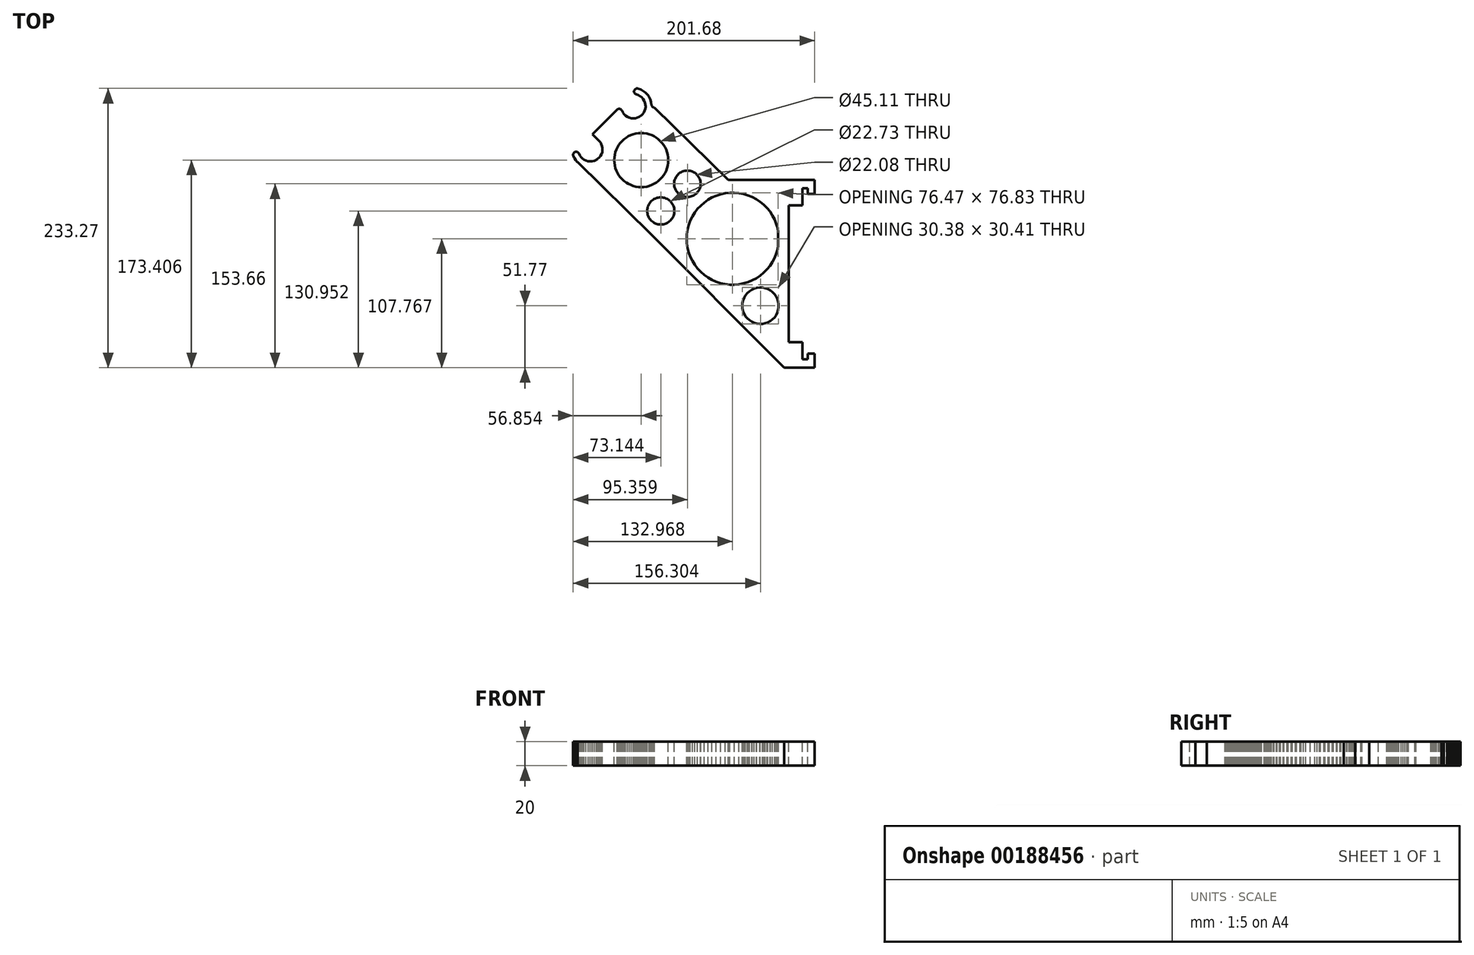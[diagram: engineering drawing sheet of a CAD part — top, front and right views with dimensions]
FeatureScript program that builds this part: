
annotation { "Feature Type Name" : "Feature", "Feature Type Description" : "" }
export const myFeature = defineFeature(function(context is Context, id is Id, definition is map)
    precondition{}
    {
        {
            var Q0;
            Q0=qCreatedBy(makeId("Top.planeOp"),FACE);
            var sketch = newSketch(context, id + "F0", { "sketchPlane" : qUnion([Q0])});
            skLineSegment(sketch, "E0", {"start": v(39.12, 12.68) * mm, "end": v(39.7, 15.67) * mm});
            skLineSegment(sketch, "E1", {"start": v(39.7, 15.67) * mm, "end": v(39.7, 16.24) * mm});
            skLineSegment(sketch, "E2", {"start": v(39.7, 16.24) * mm, "end": v(39.7, 16.28) * mm});
            skLineSegment(sketch, "E3", {"start": v(39.7, 16.28) * mm, "end": v(39.7, 16.48) * mm});
            skLineSegment(sketch, "E4", {"start": v(39.7, 16.48) * mm, "end": v(39.7, 16.55) * mm});
            skLineSegment(sketch, "E5", {"start": v(39.7, 16.55) * mm, "end": v(39.7, 16.6) * mm});
            skLineSegment(sketch, "E6", {"start": v(39.7, 16.6) * mm, "end": v(39.7, 16.7) * mm});
            skLineSegment(sketch, "E7", {"start": v(39.7, 16.7) * mm, "end": v(39.7, 16.8) * mm});
            skLineSegment(sketch, "E8", {"start": v(39.7, 16.8) * mm, "end": v(39.7, 16.95) * mm});
            skLineSegment(sketch, "E9", {"start": v(39.7, 16.95) * mm, "end": v(39.7, 17.21) * mm});
            skLineSegment(sketch, "E10", {"start": v(39.7, 17.21) * mm, "end": v(39.7, 17.9) * mm});
            skLineSegment(sketch, "E11", {"start": v(39.7, 17.9) * mm, "end": v(39.7, 18.04) * mm});
            skLineSegment(sketch, "E12", {"start": v(39.7, 18.04) * mm, "end": v(39.7, 18.74) * mm});
            skLineSegment(sketch, "E13", {"start": v(39.7, 18.74) * mm, "end": v(39.7, 21.09) * mm});
            skLineSegment(sketch, "E14", {"start": v(39.7, 21.09) * mm, "end": v(39.7, 21.12) * mm});
            skLineSegment(sketch, "E15", {"start": v(39.7, 21.12) * mm, "end": v(39.7, 21.25) * mm});
            skLineSegment(sketch, "E16", {"start": v(39.7, 21.25) * mm, "end": v(39.7, 21.3) * mm});
            skLineSegment(sketch, "E17", {"start": v(39.7, 21.3) * mm, "end": v(39.7, 23.38) * mm});
            skLineSegment(sketch, "E18", {"start": v(39.7, 23.38) * mm, "end": v(39.7, 23.5) * mm});
            skLineSegment(sketch, "E19", {"start": v(39.7, 23.5) * mm, "end": v(39.7, 26.9) * mm});
            skLineSegment(sketch, "E20", {"start": v(39.7, 26.9) * mm, "end": v(39.7, 26.97) * mm});
            skLineSegment(sketch, "E21", {"start": v(39.7, 26.97) * mm, "end": v(39.12, 29.96) * mm});
            skLineSegment(sketch, "E22", {"start": v(39.12, 29.96) * mm, "end": v(38.07, 33.67) * mm});
            skLineSegment(sketch, "E23", {"start": v(38.07, 33.67) * mm, "end": v(36.64, 37.26) * mm});
            skLineSegment(sketch, "E24", {"start": v(36.64, 37.26) * mm, "end": v(34.87, 40.7) * mm});
            skLineSegment(sketch, "E25", {"start": v(34.87, 40.7) * mm, "end": v(32.75, 43.93) * mm});
            skLineSegment(sketch, "E26", {"start": v(32.75, 43.93) * mm, "end": v(30.33, 46.93) * mm});
            skLineSegment(sketch, "E27", {"start": v(30.33, 46.93) * mm, "end": v(27.61, 49.68) * mm});
            skLineSegment(sketch, "E28", {"start": v(27.61, 49.68) * mm, "end": v(24.64, 52.14) * mm});
            skLineSegment(sketch, "E29", {"start": v(24.64, 52.14) * mm, "end": v(21.43, 54.29) * mm});
            skLineSegment(sketch, "E30", {"start": v(21.43, 54.29) * mm, "end": v(18.02, 56.1) * mm});
            skLineSegment(sketch, "E31", {"start": v(18.02, 56.1) * mm, "end": v(14.45, 57.57) * mm});
            skLineSegment(sketch, "E32", {"start": v(14.45, 57.57) * mm, "end": v(10.74, 58.67) * mm});
            skLineSegment(sketch, "E33", {"start": v(10.74, 58.67) * mm, "end": v(6.95, 59.4) * mm});
            skLineSegment(sketch, "E34", {"start": v(6.95, 59.4) * mm, "end": v(3.1, 59.73) * mm});
            skLineSegment(sketch, "E35", {"start": v(3.1, 59.73) * mm, "end": v(-0.76, 59.68) * mm});
            skLineSegment(sketch, "E36", {"start": v(-0.76, 59.68) * mm, "end": v(-4.6, 59.24) * mm});
            skLineSegment(sketch, "E37", {"start": v(-4.6, 59.24) * mm, "end": v(-8.37, 58.42) * mm});
            skLineSegment(sketch, "E38", {"start": v(-8.37, 58.42) * mm, "end": v(-12.04, 57.23) * mm});
            skLineSegment(sketch, "E39", {"start": v(-12.04, 57.23) * mm, "end": v(-15.58, 55.67) * mm});
            skLineSegment(sketch, "E40", {"start": v(-15.58, 55.67) * mm, "end": v(-18.94, 53.77) * mm});
            skLineSegment(sketch, "E41", {"start": v(-18.94, 53.77) * mm, "end": v(-22.1, 51.54) * mm});
            skLineSegment(sketch, "E42", {"start": v(-22.1, 51.54) * mm, "end": v(-25, 49) * mm});
            skLineSegment(sketch, "E43", {"start": v(-25, 49) * mm, "end": v(-27.65, 46.19) * mm});
            skLineSegment(sketch, "E44", {"start": v(-27.65, 46.19) * mm, "end": v(-30, 43.12) * mm});
            skLineSegment(sketch, "E45", {"start": v(-30, 43.12) * mm, "end": v(-32.02, 39.83) * mm});
            skLineSegment(sketch, "E46", {"start": v(-32.02, 39.83) * mm, "end": v(-33.7, 36.36) * mm});
            skLineSegment(sketch, "E47", {"start": v(-33.7, 36.36) * mm, "end": v(-35.04, 32.73) * mm});
            skLineSegment(sketch, "E48", {"start": v(-35.04, 32.73) * mm, "end": v(-36, 29) * mm});
            skLineSegment(sketch, "E49", {"start": v(-36, 29) * mm, "end": v(-36.58, 25.17) * mm});
            skLineSegment(sketch, "E50", {"start": v(-36.58, 25.17) * mm, "end": v(-36.78, 21.32) * mm});
            skLineSegment(sketch, "E51", {"start": v(-36.78, 21.32) * mm, "end": v(-36.58, 17.46) * mm});
            skLineSegment(sketch, "E52", {"start": v(-36.58, 17.46) * mm, "end": v(-36, 13.64) * mm});
            skLineSegment(sketch, "E53", {"start": v(-36, 13.64) * mm, "end": v(-35.04, 9.9) * mm});
            skLineSegment(sketch, "E54", {"start": v(-35.04, 9.9) * mm, "end": v(-33.7, 6.27) * mm});
            skLineSegment(sketch, "E55", {"start": v(-33.7, 6.27) * mm, "end": v(-32.02, 2.8) * mm});
            skLineSegment(sketch, "E56", {"start": v(-32.02, 2.8) * mm, "end": v(-30, -0.49) * mm});
            skLineSegment(sketch, "E57", {"start": v(-30, -0.49) * mm, "end": v(-27.65, -3.55) * mm});
            skLineSegment(sketch, "E58", {"start": v(-27.65, -3.55) * mm, "end": v(-25, -6.37) * mm});
            skLineSegment(sketch, "E59", {"start": v(-25, -6.37) * mm, "end": v(-22.1, -8.9) * mm});
            skLineSegment(sketch, "E60", {"start": v(-22.1, -8.9) * mm, "end": v(-18.94, -11.14) * mm});
            skLineSegment(sketch, "E61", {"start": v(-18.94, -11.14) * mm, "end": v(-15.58, -13.04) * mm});
            skLineSegment(sketch, "E62", {"start": v(-15.58, -13.04) * mm, "end": v(-12.04, -14.6) * mm});
            skLineSegment(sketch, "E63", {"start": v(-12.04, -14.6) * mm, "end": v(-8.37, -15.8) * mm});
            skLineSegment(sketch, "E64", {"start": v(-8.37, -15.8) * mm, "end": v(-4.6, -16.61) * mm});
            skLineSegment(sketch, "E65", {"start": v(-4.6, -16.61) * mm, "end": v(-0.76, -17.05) * mm});
            skLineSegment(sketch, "E66", {"start": v(-0.76, -17.05) * mm, "end": v(3.1, -17.1) * mm});
            skLineSegment(sketch, "E67", {"start": v(3.1, -17.1) * mm, "end": v(6.95, -16.76) * mm});
            skLineSegment(sketch, "E68", {"start": v(6.95, -16.76) * mm, "end": v(10.74, -16.04) * mm});
            skLineSegment(sketch, "E69", {"start": v(10.74, -16.04) * mm, "end": v(14.45, -14.94) * mm});
            skLineSegment(sketch, "E70", {"start": v(14.45, -14.94) * mm, "end": v(18.02, -13.47) * mm});
            skLineSegment(sketch, "E71", {"start": v(18.02, -13.47) * mm, "end": v(21.43, -11.65) * mm});
            skLineSegment(sketch, "E72", {"start": v(21.43, -11.65) * mm, "end": v(24.64, -9.5) * mm});
            skLineSegment(sketch, "E73", {"start": v(24.64, -9.5) * mm, "end": v(27.61, -7.04) * mm});
            skLineSegment(sketch, "E74", {"start": v(27.61, -7.04) * mm, "end": v(30.33, -4.3) * mm});
            skLineSegment(sketch, "E75", {"start": v(30.33, -4.3) * mm, "end": v(32.75, -1.3) * mm});
            skLineSegment(sketch, "E76", {"start": v(32.75, -1.3) * mm, "end": v(34.87, 1.94) * mm});
            skLineSegment(sketch, "E77", {"start": v(34.87, 1.94) * mm, "end": v(36.64, 5.37) * mm});
            skLineSegment(sketch, "E78", {"start": v(36.64, 5.37) * mm, "end": v(38.07, 8.96) * mm});
            skLineSegment(sketch, "E79", {"start": v(38.07, 8.96) * mm, "end": v(39.12, 12.68) * mm});
            skLineSegment(sketch, "E80", {"start": v(-110.95, 88) * mm, "end": v(-110.88, 88.06) * mm});
            skLineSegment(sketch, "E81", {"start": v(-110.88, 88.06) * mm, "end": v(-109.69, 89.17) * mm});
            skLineSegment(sketch, "E82", {"start": v(-109.69, 89.17) * mm, "end": v(-109.62, 89.23) * mm});
            skLineSegment(sketch, "E83", {"start": v(-109.62, 89.23) * mm, "end": v(-108.63, 90.52) * mm});
            skLineSegment(sketch, "E84", {"start": v(-108.63, 90.52) * mm, "end": v(-108.58, 90.59) * mm});
            skLineSegment(sketch, "E85", {"start": v(-108.58, 90.59) * mm, "end": v(-107.82, 92.03) * mm});
            skLineSegment(sketch, "E86", {"start": v(-107.82, 92.03) * mm, "end": v(-107.78, 92.1) * mm});
            skLineSegment(sketch, "E87", {"start": v(-107.78, 92.1) * mm, "end": v(-107.28, 93.66) * mm});
            skLineSegment(sketch, "E88", {"start": v(-107.28, 93.66) * mm, "end": v(-107.25, 93.74) * mm});
            skLineSegment(sketch, "E89", {"start": v(-107.25, 93.74) * mm, "end": v(-107.01, 95.36) * mm});
            skLineSegment(sketch, "E90", {"start": v(-107.01, 95.36) * mm, "end": v(-107, 95.44) * mm});
            skLineSegment(sketch, "E91", {"start": v(-107, 95.44) * mm, "end": v(-107.04, 97.07) * mm});
            skLineSegment(sketch, "E92", {"start": v(-107.04, 97.07) * mm, "end": v(-107.04, 97.16) * mm});
            skLineSegment(sketch, "E93", {"start": v(-107.04, 97.16) * mm, "end": v(-107.36, 98.76) * mm});
            skLineSegment(sketch, "E94", {"start": v(-107.36, 98.76) * mm, "end": v(-107.37, 98.84) * mm});
            skLineSegment(sketch, "E95", {"start": v(-107.37, 98.84) * mm, "end": v(-107.95, 100.37) * mm});
            skLineSegment(sketch, "E96", {"start": v(-107.95, 100.37) * mm, "end": v(-107.98, 100.45) * mm});
            skLineSegment(sketch, "E97", {"start": v(-107.98, 100.45) * mm, "end": v(-108.8, 101.85) * mm});
            skLineSegment(sketch, "E98", {"start": v(-108.8, 101.85) * mm, "end": v(-108.85, 101.93) * mm});
            skLineSegment(sketch, "E99", {"start": v(-108.85, 101.93) * mm, "end": v(-109.9, 103.17) * mm});
            skLineSegment(sketch, "E100", {"start": v(-109.9, 103.17) * mm, "end": v(-109.96, 103.24) * mm});
            skLineSegment(sketch, "E101", {"start": v(-109.96, 103.24) * mm, "end": v(-110.23, 103.5) * mm});
            skLineSegment(sketch, "E102", {"start": v(-110.23, 103.5) * mm, "end": v(-115.35, 108.63) * mm});
            skLineSegment(sketch, "E103", {"start": v(-115.35, 108.63) * mm, "end": v(-114.32, 109.65) * mm});
            skLineSegment(sketch, "E104", {"start": v(-114.32, 109.65) * mm, "end": v(-94.84, 129.13) * mm});
            skLineSegment(sketch, "E105", {"start": v(-94.84, 129.13) * mm, "end": v(-94.52, 129.4) * mm});
            skLineSegment(sketch, "E106", {"start": v(-94.52, 129.4) * mm, "end": v(-94.16, 129.62) * mm});
            skLineSegment(sketch, "E107", {"start": v(-94.16, 129.62) * mm, "end": v(-93.77, 129.77) * mm});
            skLineSegment(sketch, "E108", {"start": v(-93.77, 129.77) * mm, "end": v(-93.36, 129.86) * mm});
            skLineSegment(sketch, "E109", {"start": v(-93.36, 129.86) * mm, "end": v(-92.94, 129.88) * mm});
            skLineSegment(sketch, "E110", {"start": v(-92.94, 129.88) * mm, "end": v(-92.53, 129.83) * mm});
            skLineSegment(sketch, "E111", {"start": v(-92.53, 129.83) * mm, "end": v(-92.12, 129.7) * mm});
            skLineSegment(sketch, "E112", {"start": v(-92.12, 129.7) * mm, "end": v(-91.75, 129.52) * mm});
            skLineSegment(sketch, "E113", {"start": v(-91.75, 129.52) * mm, "end": v(-91.4, 129.28) * mm});
            skLineSegment(sketch, "E114", {"start": v(-91.4, 129.28) * mm, "end": v(-91.1, 128.98) * mm});
            skLineSegment(sketch, "E115", {"start": v(-91.1, 128.98) * mm, "end": v(-90.87, 128.64) * mm});
            skLineSegment(sketch, "E116", {"start": v(-90.87, 128.64) * mm, "end": v(-90.68, 128.27) * mm});
            skLineSegment(sketch, "E117", {"start": v(-90.68, 128.27) * mm, "end": v(-89.95, 126.8) * mm});
            skLineSegment(sketch, "E118", {"start": v(-89.95, 126.8) * mm, "end": v(-89.91, 126.72) * mm});
            skLineSegment(sketch, "E119", {"start": v(-89.91, 126.72) * mm, "end": v(-88.95, 125.39) * mm});
            skLineSegment(sketch, "E120", {"start": v(-88.95, 125.39) * mm, "end": v(-88.9, 125.32) * mm});
            skLineSegment(sketch, "E121", {"start": v(-88.9, 125.32) * mm, "end": v(-87.72, 124.17) * mm});
            skLineSegment(sketch, "E122", {"start": v(-87.72, 124.17) * mm, "end": v(-87.66, 124.11) * mm});
            skLineSegment(sketch, "E123", {"start": v(-87.66, 124.11) * mm, "end": v(-86.3, 123.19) * mm});
            skLineSegment(sketch, "E124", {"start": v(-86.3, 123.19) * mm, "end": v(-86.23, 123.14) * mm});
            skLineSegment(sketch, "E125", {"start": v(-86.23, 123.14) * mm, "end": v(-84.74, 122.45) * mm});
            skLineSegment(sketch, "E126", {"start": v(-84.74, 122.45) * mm, "end": v(-84.66, 122.42) * mm});
            skLineSegment(sketch, "E127", {"start": v(-84.66, 122.42) * mm, "end": v(-83.07, 122) * mm});
            skLineSegment(sketch, "E128", {"start": v(-83.07, 122) * mm, "end": v(-82.99, 121.97) * mm});
            skLineSegment(sketch, "E129", {"start": v(-82.99, 121.97) * mm, "end": v(-81.35, 121.83) * mm});
            skLineSegment(sketch, "E130", {"start": v(-81.35, 121.83) * mm, "end": v(-81.27, 121.82) * mm});
            skLineSegment(sketch, "E131", {"start": v(-81.27, 121.82) * mm, "end": v(-79.63, 121.95) * mm});
            skLineSegment(sketch, "E132", {"start": v(-79.63, 121.95) * mm, "end": v(-79.54, 121.96) * mm});
            skLineSegment(sketch, "E133", {"start": v(-79.54, 121.96) * mm, "end": v(-77.95, 122.37) * mm});
            skLineSegment(sketch, "E134", {"start": v(-77.95, 122.37) * mm, "end": v(-77.87, 122.39) * mm});
            skLineSegment(sketch, "E135", {"start": v(-77.87, 122.39) * mm, "end": v(-76.37, 123.06) * mm});
            skLineSegment(sketch, "E136", {"start": v(-76.37, 123.06) * mm, "end": v(-76.3, 123.1) * mm});
            skLineSegment(sketch, "E137", {"start": v(-76.3, 123.1) * mm, "end": v(-74.93, 124.01) * mm});
            skLineSegment(sketch, "E138", {"start": v(-74.93, 124.01) * mm, "end": v(-74.86, 124.06) * mm});
            skLineSegment(sketch, "E139", {"start": v(-74.86, 124.06) * mm, "end": v(-73.67, 125.2) * mm});
            skLineSegment(sketch, "E140", {"start": v(-73.67, 125.2) * mm, "end": v(-73.6, 125.25) * mm});
            skLineSegment(sketch, "E141", {"start": v(-73.6, 125.25) * mm, "end": v(-72.63, 126.57) * mm});
            skLineSegment(sketch, "E142", {"start": v(-72.63, 126.57) * mm, "end": v(-72.58, 126.64) * mm});
            skLineSegment(sketch, "E143", {"start": v(-72.58, 126.64) * mm, "end": v(-71.84, 128.1) * mm});
            skLineSegment(sketch, "E144", {"start": v(-71.84, 128.1) * mm, "end": v(-71.8, 128.19) * mm});
            skLineSegment(sketch, "E145", {"start": v(-71.8, 128.19) * mm, "end": v(-71.32, 129.76) * mm});
            skLineSegment(sketch, "E146", {"start": v(-71.32, 129.76) * mm, "end": v(-71.3, 129.84) * mm});
            skLineSegment(sketch, "E147", {"start": v(-71.3, 129.84) * mm, "end": v(-71.08, 131.47) * mm});
            skLineSegment(sketch, "E148", {"start": v(-71.08, 131.47) * mm, "end": v(-71.07, 131.55) * mm});
            skLineSegment(sketch, "E149", {"start": v(-71.07, 131.55) * mm, "end": v(-71.14, 133.2) * mm});
            skLineSegment(sketch, "E150", {"start": v(-71.14, 133.2) * mm, "end": v(-71.15, 133.28) * mm});
            skLineSegment(sketch, "E151", {"start": v(-71.15, 133.28) * mm, "end": v(-71.5, 134.89) * mm});
            skLineSegment(sketch, "E152", {"start": v(-71.5, 134.89) * mm, "end": v(-71.51, 134.97) * mm});
            skLineSegment(sketch, "E153", {"start": v(-71.51, 134.97) * mm, "end": v(-72.13, 136.5) * mm});
            skLineSegment(sketch, "E154", {"start": v(-72.13, 136.5) * mm, "end": v(-72.16, 136.57) * mm});
            skLineSegment(sketch, "E155", {"start": v(-72.16, 136.57) * mm, "end": v(-73.03, 137.97) * mm});
            skLineSegment(sketch, "E156", {"start": v(-73.03, 137.97) * mm, "end": v(-73.07, 138.04) * mm});
            skLineSegment(sketch, "E157", {"start": v(-73.07, 138.04) * mm, "end": v(-74.16, 139.27) * mm});
            skLineSegment(sketch, "E158", {"start": v(-74.16, 139.27) * mm, "end": v(-74.22, 139.34) * mm});
            skLineSegment(sketch, "E159", {"start": v(-74.22, 139.34) * mm, "end": v(-75.5, 140.37) * mm});
            skLineSegment(sketch, "E160", {"start": v(-75.5, 140.37) * mm, "end": v(-75.57, 140.42) * mm});
            skLineSegment(sketch, "E161", {"start": v(-75.57, 140.42) * mm, "end": v(-77, 141.21) * mm});
            skLineSegment(sketch, "E162", {"start": v(-77, 141.21) * mm, "end": v(-77.08, 141.26) * mm});
            skLineSegment(sketch, "E163", {"start": v(-77.08, 141.26) * mm, "end": v(-78.63, 141.8) * mm});
            skLineSegment(sketch, "E164", {"start": v(-78.63, 141.8) * mm, "end": v(-78.72, 141.82) * mm});
            skLineSegment(sketch, "E165", {"start": v(-78.72, 141.82) * mm, "end": v(-79.13, 141.97) * mm});
            skLineSegment(sketch, "E166", {"start": v(-79.13, 141.97) * mm, "end": v(-79.52, 142.19) * mm});
            skLineSegment(sketch, "E167", {"start": v(-79.52, 142.19) * mm, "end": v(-79.86, 142.47) * mm});
            skLineSegment(sketch, "E168", {"start": v(-79.86, 142.47) * mm, "end": v(-80.15, 142.8) * mm});
            skLineSegment(sketch, "E169", {"start": v(-80.15, 142.8) * mm, "end": v(-80.38, 143.18) * mm});
            skLineSegment(sketch, "E170", {"start": v(-80.38, 143.18) * mm, "end": v(-80.53, 143.6) * mm});
            skLineSegment(sketch, "E171", {"start": v(-80.53, 143.6) * mm, "end": v(-80.62, 144.03) * mm});
            skLineSegment(sketch, "E172", {"start": v(-80.62, 144.03) * mm, "end": v(-80.62, 144.47) * mm});
            skLineSegment(sketch, "E173", {"start": v(-80.62, 144.47) * mm, "end": v(-80.55, 144.91) * mm});
            skLineSegment(sketch, "E174", {"start": v(-80.55, 144.91) * mm, "end": v(-80.4, 145.33) * mm});
            skLineSegment(sketch, "E175", {"start": v(-80.4, 145.33) * mm, "end": v(-80.19, 145.72) * mm});
            skLineSegment(sketch, "E176", {"start": v(-80.19, 145.72) * mm, "end": v(-79.9, 146.06) * mm});
            skLineSegment(sketch, "E177", {"start": v(-79.9, 146.06) * mm, "end": v(-79.57, 146.35) * mm});
            skLineSegment(sketch, "E178", {"start": v(-79.57, 146.35) * mm, "end": v(-79.2, 146.57) * mm});
            skLineSegment(sketch, "E179", {"start": v(-79.2, 146.57) * mm, "end": v(-78.78, 146.73) * mm});
            skLineSegment(sketch, "E180", {"start": v(-78.78, 146.73) * mm, "end": v(-78.34, 146.81) * mm});
            skLineSegment(sketch, "E181", {"start": v(-78.34, 146.81) * mm, "end": v(-77.9, 146.82) * mm});
            skLineSegment(sketch, "E182", {"start": v(-77.9, 146.82) * mm, "end": v(-77.46, 146.75) * mm});
            skLineSegment(sketch, "E183", {"start": v(-77.46, 146.75) * mm, "end": v(-77.35, 146.7) * mm});
            skLineSegment(sketch, "E184", {"start": v(-77.35, 146.7) * mm, "end": v(-75.22, 145.98) * mm});
            skLineSegment(sketch, "E185", {"start": v(-75.22, 145.98) * mm, "end": v(-75.11, 145.93) * mm});
            skLineSegment(sketch, "E186", {"start": v(-75.11, 145.93) * mm, "end": v(-73.12, 144.88) * mm});
            skLineSegment(sketch, "E187", {"start": v(-73.12, 144.88) * mm, "end": v(-73.02, 144.81) * mm});
            skLineSegment(sketch, "E188", {"start": v(-73.02, 144.81) * mm, "end": v(-71.21, 143.47) * mm});
            skLineSegment(sketch, "E189", {"start": v(-71.21, 143.47) * mm, "end": v(-71.13, 143.38) * mm});
            skLineSegment(sketch, "E190", {"start": v(-71.13, 143.38) * mm, "end": v(-69.55, 141.77) * mm});
            skLineSegment(sketch, "E191", {"start": v(-69.55, 141.77) * mm, "end": v(-69.48, 141.68) * mm});
            skLineSegment(sketch, "E192", {"start": v(-69.48, 141.68) * mm, "end": v(-68.17, 139.84) * mm});
            skLineSegment(sketch, "E193", {"start": v(-68.17, 139.84) * mm, "end": v(-68.12, 139.74) * mm});
            skLineSegment(sketch, "E194", {"start": v(-68.12, 139.74) * mm, "end": v(-67.1, 137.72) * mm});
            skLineSegment(sketch, "E195", {"start": v(-67.1, 137.72) * mm, "end": v(-67.07, 137.61) * mm});
            skLineSegment(sketch, "E196", {"start": v(-67.07, 137.61) * mm, "end": v(-66.39, 135.46) * mm});
            skLineSegment(sketch, "E197", {"start": v(-66.39, 135.46) * mm, "end": v(-66.37, 135.35) * mm});
            skLineSegment(sketch, "E198", {"start": v(-66.37, 135.35) * mm, "end": v(-66.03, 133.12) * mm});
            skLineSegment(sketch, "E199", {"start": v(-66.03, 133.12) * mm, "end": v(-65.96, 132.72) * mm});
            skLineSegment(sketch, "E200", {"start": v(-65.96, 132.72) * mm, "end": v(-65.83, 132.32) * mm});
            skLineSegment(sketch, "E201", {"start": v(-65.83, 132.32) * mm, "end": v(-65.64, 131.95) * mm});
            skLineSegment(sketch, "E202", {"start": v(-65.64, 131.95) * mm, "end": v(-65.38, 131.61) * mm});
            skLineSegment(sketch, "E203", {"start": v(-65.38, 131.61) * mm, "end": v(-65.08, 131.32) * mm});
            skLineSegment(sketch, "E204", {"start": v(-65.08, 131.32) * mm, "end": v(-64.72, 131.1) * mm});
            skLineSegment(sketch, "E205", {"start": v(-64.72, 131.1) * mm, "end": v(-64.34, 130.92) * mm});
            skLineSegment(sketch, "E206", {"start": v(-64.34, 130.92) * mm, "end": v(-63.93, 130.8) * mm});
            skLineSegment(sketch, "E207", {"start": v(-63.93, 130.8) * mm, "end": v(-63.51, 130.77) * mm});
            skLineSegment(sketch, "E208", {"start": v(-2.18, 70.4) * mm, "end": v(1.46, 70.4) * mm});
            skLineSegment(sketch, "E209", {"start": v(1.46, 70.4) * mm, "end": v(70.17, 70.4) * mm});
            skLineSegment(sketch, "E210", {"start": v(70.17, 70.4) * mm, "end": v(70.17, 69.81) * mm});
            skLineSegment(sketch, "E211", {"start": v(70.17, 69.81) * mm, "end": v(70.17, 58.65) * mm});
            skLineSegment(sketch, "E212", {"start": v(70.17, 58.65) * mm, "end": v(69.88, 58.65) * mm});
            skLineSegment(sketch, "E213", {"start": v(69.88, 58.65) * mm, "end": v(64.46, 58.65) * mm});
            skLineSegment(sketch, "E214", {"start": v(64.46, 58.65) * mm, "end": v(64.46, 58.9) * mm});
            skLineSegment(sketch, "E215", {"start": v(64.46, 58.9) * mm, "end": v(64.46, 60.87) * mm});
            skLineSegment(sketch, "E216", {"start": v(64.46, 60.87) * mm, "end": v(64.46, 61.36) * mm});
            skLineSegment(sketch, "E217", {"start": v(64.46, 61.36) * mm, "end": v(64.46, 62.15) * mm});
            skLineSegment(sketch, "E218", {"start": v(64.46, 62.15) * mm, "end": v(64.46, 63.44) * mm});
            skLineSegment(sketch, "E219", {"start": v(64.46, 63.44) * mm, "end": v(60.01, 63.44) * mm});
            skLineSegment(sketch, "E220", {"start": v(60.01, 63.44) * mm, "end": v(60.01, 60.16) * mm});
            skLineSegment(sketch, "E221", {"start": v(60.01, 60.16) * mm, "end": v(60.01, 58.1) * mm});
            skLineSegment(sketch, "E222", {"start": v(60.01, 58.1) * mm, "end": v(60.01, 49.13) * mm});
            skLineSegment(sketch, "E223", {"start": v(60.01, 49.13) * mm, "end": v(53.66, 49.13) * mm});
            skLineSegment(sketch, "E224", {"start": v(53.66, 49.13) * mm, "end": v(48.58, 49.13) * mm});
            skLineSegment(sketch, "E225", {"start": v(48.58, 49.13) * mm, "end": v(48.58, -9.3) * mm});
            skLineSegment(sketch, "E226", {"start": v(48.58, -9.3) * mm, "end": v(48.58, -65.17) * mm});
            skLineSegment(sketch, "E227", {"start": v(48.58, -65.17) * mm, "end": v(54.93, -65.17) * mm});
            skLineSegment(sketch, "E228", {"start": v(54.93, -65.17) * mm, "end": v(60.01, -65.17) * mm});
            skLineSegment(sketch, "E229", {"start": v(60.01, -65.17) * mm, "end": v(60.01, -72.8) * mm});
            skLineSegment(sketch, "E230", {"start": v(60.01, -72.8) * mm, "end": v(60.01, -74.15) * mm});
            skLineSegment(sketch, "E231", {"start": v(60.01, -74.15) * mm, "end": v(60.01, -76.21) * mm});
            skLineSegment(sketch, "E232", {"start": v(60.01, -76.21) * mm, "end": v(60.01, -79.48) * mm});
            skLineSegment(sketch, "E233", {"start": v(60.01, -79.48) * mm, "end": v(64.46, -79.48) * mm});
            skLineSegment(sketch, "E234", {"start": v(64.46, -79.48) * mm, "end": v(64.46, -78.2) * mm});
            skLineSegment(sketch, "E235", {"start": v(64.46, -78.2) * mm, "end": v(64.46, -77.41) * mm});
            skLineSegment(sketch, "E236", {"start": v(64.46, -77.41) * mm, "end": v(64.46, -76.92) * mm});
            skLineSegment(sketch, "E237", {"start": v(64.46, -76.92) * mm, "end": v(64.46, -74.7) * mm});
            skLineSegment(sketch, "E238", {"start": v(64.46, -74.7) * mm, "end": v(64.74, -74.7) * mm});
            skLineSegment(sketch, "E239", {"start": v(64.74, -74.7) * mm, "end": v(70.17, -74.7) * mm});
            skLineSegment(sketch, "E240", {"start": v(70.17, -74.7) * mm, "end": v(70.17, -75.29) * mm});
            skLineSegment(sketch, "E241", {"start": v(70.17, -75.29) * mm, "end": v(70.17, -86.45) * mm});
            skLineSegment(sketch, "E242", {"start": v(70.17, -86.45) * mm, "end": v(68.9, -86.45) * mm});
            skLineSegment(sketch, "E243", {"start": v(68.9, -86.45) * mm, "end": v(44.77, -86.45) * mm});
            skLineSegment(sketch, "E244", {"start": v(44.77, -86.45) * mm, "end": v(39.2, -80.88) * mm});
            skLineSegment(sketch, "E245", {"start": v(39.2, -80.88) * mm, "end": v(-66.58, 24.9) * mm});
            skLineSegment(sketch, "E246", {"start": v(-127.92, 85.28) * mm, "end": v(-127.99, 85.36) * mm});
            skLineSegment(sketch, "E247", {"start": v(-127.99, 85.36) * mm, "end": v(-129.3, 86.85) * mm});
            skLineSegment(sketch, "E248", {"start": v(-129.3, 86.85) * mm, "end": v(-129.35, 86.94) * mm});
            skLineSegment(sketch, "E249", {"start": v(-129.35, 86.94) * mm, "end": v(-130.44, 88.6) * mm});
            skLineSegment(sketch, "E250", {"start": v(-130.44, 88.6) * mm, "end": v(-130.48, 88.7) * mm});
            skLineSegment(sketch, "E251", {"start": v(-130.48, 88.7) * mm, "end": v(-131.33, 90.5) * mm});
            skLineSegment(sketch, "E252", {"start": v(-131.33, 90.5) * mm, "end": v(-131.46, 90.91) * mm});
            skLineSegment(sketch, "E253", {"start": v(-131.46, 90.91) * mm, "end": v(-131.5, 91.35) * mm});
            skLineSegment(sketch, "E254", {"start": v(-131.5, 91.35) * mm, "end": v(-131.48, 91.8) * mm});
            skLineSegment(sketch, "E255", {"start": v(-131.48, 91.8) * mm, "end": v(-131.37, 92.23) * mm});
            skLineSegment(sketch, "E256", {"start": v(-131.37, 92.23) * mm, "end": v(-131.2, 92.63) * mm});
            skLineSegment(sketch, "E257", {"start": v(-131.2, 92.63) * mm, "end": v(-130.95, 93) * mm});
            skLineSegment(sketch, "E258", {"start": v(-130.95, 93) * mm, "end": v(-130.65, 93.32) * mm});
            skLineSegment(sketch, "E259", {"start": v(-130.65, 93.32) * mm, "end": v(-130.3, 93.59) * mm});
            skLineSegment(sketch, "E260", {"start": v(-130.3, 93.59) * mm, "end": v(-129.9, 93.78) * mm});
            skLineSegment(sketch, "E261", {"start": v(-129.9, 93.78) * mm, "end": v(-129.47, 93.9) * mm});
            skLineSegment(sketch, "E262", {"start": v(-129.47, 93.9) * mm, "end": v(-129.03, 93.96) * mm});
            skLineSegment(sketch, "E263", {"start": v(-129.03, 93.96) * mm, "end": v(-128.59, 93.93) * mm});
            skLineSegment(sketch, "E264", {"start": v(-128.59, 93.93) * mm, "end": v(-128.16, 93.83) * mm});
            skLineSegment(sketch, "E265", {"start": v(-128.16, 93.83) * mm, "end": v(-127.75, 93.65) * mm});
            skLineSegment(sketch, "E266", {"start": v(-127.75, 93.65) * mm, "end": v(-127.38, 93.4) * mm});
            skLineSegment(sketch, "E267", {"start": v(-127.38, 93.4) * mm, "end": v(-127.06, 93.1) * mm});
            skLineSegment(sketch, "E268", {"start": v(-127.06, 93.1) * mm, "end": v(-126.8, 92.74) * mm});
            skLineSegment(sketch, "E269", {"start": v(-126.8, 92.74) * mm, "end": v(-126.6, 92.35) * mm});
            skLineSegment(sketch, "E270", {"start": v(-126.6, 92.35) * mm, "end": v(-125.88, 90.88) * mm});
            skLineSegment(sketch, "E271", {"start": v(-125.88, 90.88) * mm, "end": v(-125.84, 90.8) * mm});
            skLineSegment(sketch, "E272", {"start": v(-125.84, 90.8) * mm, "end": v(-124.88, 89.49) * mm});
            skLineSegment(sketch, "E273", {"start": v(-124.88, 89.49) * mm, "end": v(-124.83, 89.42) * mm});
            skLineSegment(sketch, "E274", {"start": v(-124.83, 89.42) * mm, "end": v(-123.67, 88.28) * mm});
            skLineSegment(sketch, "E275", {"start": v(-123.67, 88.28) * mm, "end": v(-123.6, 88.22) * mm});
            skLineSegment(sketch, "E276", {"start": v(-123.6, 88.22) * mm, "end": v(-122.26, 87.29) * mm});
            skLineSegment(sketch, "E277", {"start": v(-122.26, 87.29) * mm, "end": v(-122.2, 87.24) * mm});
            skLineSegment(sketch, "E278", {"start": v(-122.2, 87.24) * mm, "end": v(-120.71, 86.55) * mm});
            skLineSegment(sketch, "E279", {"start": v(-120.71, 86.55) * mm, "end": v(-120.64, 86.52) * mm});
            skLineSegment(sketch, "E280", {"start": v(-120.64, 86.52) * mm, "end": v(-119.06, 86.09) * mm});
            skLineSegment(sketch, "E281", {"start": v(-119.06, 86.09) * mm, "end": v(-118.98, 86.06) * mm});
            skLineSegment(sketch, "E282", {"start": v(-118.98, 86.06) * mm, "end": v(-117.36, 85.9) * mm});
            skLineSegment(sketch, "E283", {"start": v(-117.36, 85.9) * mm, "end": v(-117.27, 85.9) * mm});
            skLineSegment(sketch, "E284", {"start": v(-117.27, 85.9) * mm, "end": v(-115.64, 86.01) * mm});
            skLineSegment(sketch, "E285", {"start": v(-115.64, 86.01) * mm, "end": v(-115.56, 86.02) * mm});
            skLineSegment(sketch, "E286", {"start": v(-115.56, 86.02) * mm, "end": v(-113.97, 86.41) * mm});
            skLineSegment(sketch, "E287", {"start": v(-113.97, 86.41) * mm, "end": v(-113.9, 86.43) * mm});
            skLineSegment(sketch, "E288", {"start": v(-113.9, 86.43) * mm, "end": v(-112.4, 87.08) * mm});
            skLineSegment(sketch, "E289", {"start": v(-112.4, 87.08) * mm, "end": v(-112.32, 87.12) * mm});
            skLineSegment(sketch, "E290", {"start": v(-112.32, 87.12) * mm, "end": v(-110.95, 88) * mm});
            skLineSegment(sketch, "E291", {"start": v(9.78, -37) * mm, "end": v(9.6, -34.68) * mm});
            skLineSegment(sketch, "E292", {"start": v(9.6, -34.68) * mm, "end": v(9.78, -32.36) * mm});
            skLineSegment(sketch, "E293", {"start": v(9.78, -32.36) * mm, "end": v(10.31, -30.1) * mm});
            skLineSegment(sketch, "E294", {"start": v(10.31, -30.1) * mm, "end": v(11.18, -27.93) * mm});
            skLineSegment(sketch, "E295", {"start": v(11.18, -27.93) * mm, "end": v(12.37, -25.93) * mm});
            skLineSegment(sketch, "E296", {"start": v(12.37, -25.93) * mm, "end": v(13.85, -24.13) * mm});
            skLineSegment(sketch, "E297", {"start": v(13.85, -24.13) * mm, "end": v(15.6, -22.58) * mm});
            skLineSegment(sketch, "E298", {"start": v(15.6, -22.58) * mm, "end": v(17.55, -21.31) * mm});
            skLineSegment(sketch, "E299", {"start": v(17.55, -21.31) * mm, "end": v(19.67, -20.36) * mm});
            skLineSegment(sketch, "E300", {"start": v(19.67, -20.36) * mm, "end": v(21.92, -19.74) * mm});
            skLineSegment(sketch, "E301", {"start": v(21.92, -19.74) * mm, "end": v(24.23, -19.48) * mm});
            skLineSegment(sketch, "E302", {"start": v(24.23, -19.48) * mm, "end": v(26.56, -19.57) * mm});
            skLineSegment(sketch, "E303", {"start": v(26.56, -19.57) * mm, "end": v(28.85, -20) * mm});
            skLineSegment(sketch, "E304", {"start": v(28.85, -20) * mm, "end": v(31.04, -20.8) * mm});
            skLineSegment(sketch, "E305", {"start": v(31.04, -20.8) * mm, "end": v(33.09, -21.91) * mm});
            skLineSegment(sketch, "E306", {"start": v(33.09, -21.91) * mm, "end": v(34.94, -23.32) * mm});
            skLineSegment(sketch, "E307", {"start": v(34.94, -23.32) * mm, "end": v(36.55, -25) * mm});
            skLineSegment(sketch, "E308", {"start": v(36.55, -25) * mm, "end": v(37.9, -26.9) * mm});
            skLineSegment(sketch, "E309", {"start": v(37.9, -26.9) * mm, "end": v(38.93, -29) * mm});
            skLineSegment(sketch, "E310", {"start": v(38.93, -29) * mm, "end": v(39.63, -31.21) * mm});
            skLineSegment(sketch, "E311", {"start": v(39.63, -31.21) * mm, "end": v(39.99, -33.52) * mm});
            skLineSegment(sketch, "E312", {"start": v(39.99, -33.52) * mm, "end": v(39.99, -35.85) * mm});
            skLineSegment(sketch, "E313", {"start": v(39.99, -35.85) * mm, "end": v(39.63, -38.15) * mm});
            skLineSegment(sketch, "E314", {"start": v(39.63, -38.15) * mm, "end": v(38.93, -40.37) * mm});
            skLineSegment(sketch, "E315", {"start": v(38.93, -40.37) * mm, "end": v(37.9, -42.46) * mm});
            skLineSegment(sketch, "E316", {"start": v(37.9, -42.46) * mm, "end": v(36.55, -44.36) * mm});
            skLineSegment(sketch, "E317", {"start": v(36.55, -44.36) * mm, "end": v(34.94, -46.04) * mm});
            skLineSegment(sketch, "E318", {"start": v(34.94, -46.04) * mm, "end": v(33.09, -47.45) * mm});
            skLineSegment(sketch, "E319", {"start": v(33.09, -47.45) * mm, "end": v(31.04, -48.56) * mm});
            skLineSegment(sketch, "E320", {"start": v(31.04, -48.56) * mm, "end": v(28.85, -49.35) * mm});
            skLineSegment(sketch, "E321", {"start": v(28.85, -49.35) * mm, "end": v(26.56, -49.8) * mm});
            skLineSegment(sketch, "E322", {"start": v(26.56, -49.8) * mm, "end": v(24.23, -49.88) * mm});
            skLineSegment(sketch, "E323", {"start": v(24.23, -49.88) * mm, "end": v(21.92, -49.62) * mm});
            skLineSegment(sketch, "E324", {"start": v(21.92, -49.62) * mm, "end": v(19.67, -49) * mm});
            skLineSegment(sketch, "E325", {"start": v(19.67, -49) * mm, "end": v(17.55, -48.05) * mm});
            skLineSegment(sketch, "E326", {"start": v(17.55, -48.05) * mm, "end": v(15.6, -46.78) * mm});
            skLineSegment(sketch, "E327", {"start": v(15.6, -46.78) * mm, "end": v(13.85, -45.23) * mm});
            skLineSegment(sketch, "E328", {"start": v(13.85, -45.23) * mm, "end": v(12.37, -43.43) * mm});
            skLineSegment(sketch, "E329", {"start": v(12.37, -43.43) * mm, "end": v(11.18, -41.43) * mm});
            skLineSegment(sketch, "E330", {"start": v(11.18, -41.43) * mm, "end": v(10.31, -39.27) * mm});
            skLineSegment(sketch, "E331", {"start": v(10.31, -39.27) * mm, "end": v(9.78, -37) * mm});
            skLineSegment(sketch, "E332", {"start": v(-66.58, 24.9) * mm, "end": v(-127.92, 85.28) * mm});
            skLineSegment(sketch, "E333", {"start": v(-2.18, 70.4) * mm, "end": v(-63.51, 130.77) * mm});
            skSolve(sketch);
        }
        {
            var Q0;
            Q0=makeQuery(id+"F0.imprint","IMPRINT",FACE,{"disambiguationData":[TD([[makeQuery(id+"F0.imprint","IMPRINT",EDGE,{"derivedFrom":sQuery(id+"F0.wireOp",EDGE,"E0")}),-1.0]])]});
            var sketch = newSketch(context, id + "F1", { "sketchPlane" : qUnion([Q0])});
            skCircle(sketch, "E334", {"center": v(-74.66, 86.96) * mm, "radius": 22.56 * mm});
            skCircle(sketch, "E335", {"center": v(-58.37, 44.5) * mm, "radius": 11.36 * mm});
            skCircle(sketch, "E336", {"center": v(-36.15, 67.2) * mm, "radius": 11.04 * mm});
            skSolve(sketch);
        }
        {
            var Q0;
            Q0=makeQuery(id+"F0.imprint","IMPRINT",FACE,{"disambiguationData":[TD([[makeQuery(id+"F0.imprint","IMPRINT",EDGE,{"derivedFrom":sQuery(id+"F0.wireOp",EDGE,"E0")}),-1.0]])]});
            extrude(context, id + "F2", {"entities" : qUnion([Q0]), "oppositeDirection" : true, "depth" : 20 * mm});
        }
        {
            var Q0;
            Q0=makeQuery(id+"F1.imprint","IMPRINT",FACE,{"disambiguationData":[TD([[makeQuery(id+"F1.imprint","IMPRINT",EDGE,{"derivedFrom":sQuery(id+"F1.wireOp",EDGE,"E334")}),1.0]])]});
            var Q1;
            Q1=makeQuery(id+"F1.imprint","IMPRINT",FACE,{"disambiguationData":[TD([[makeQuery(id+"F1.imprint","IMPRINT",EDGE,{"derivedFrom":sQuery(id+"F1.wireOp",EDGE,"E335")}),1.0]])]});
            var Q2;
            Q2=makeQuery(id+"F1.imprint","IMPRINT",FACE,{"disambiguationData":[TD([[makeQuery(id+"F1.imprint","IMPRINT",EDGE,{"derivedFrom":sQuery(id+"F1.wireOp",EDGE,"E336")}),1.0]])]});
            extrude(context, id + "F3", {"entities" : qUnion([Q0, Q1, Q2]), "operationType" : NewBodyOperationType.REMOVE, "endBound" : BoundingType.THROUGH_ALL, "oppositeDirection" : true, "depth" : 25 * mm});
        }
    });
